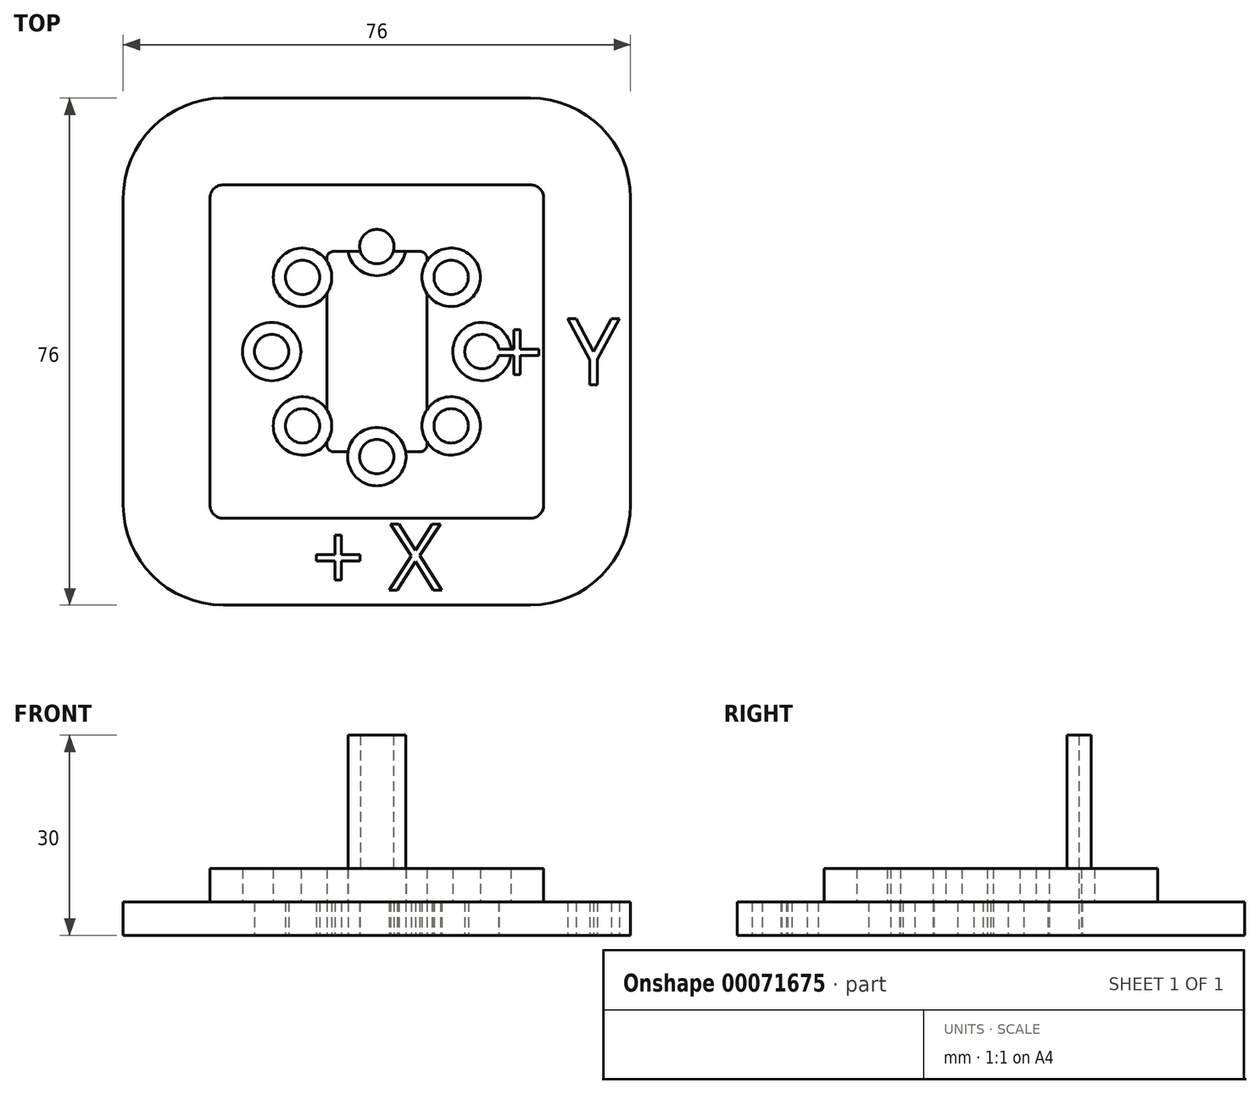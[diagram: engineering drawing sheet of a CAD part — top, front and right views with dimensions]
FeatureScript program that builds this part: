
annotation { "Feature Type Name" : "Feature", "Feature Type Description" : "" }
export const myFeature = defineFeature(function(context is Context, id is Id, definition is map)
    precondition{}
    {
        {
            var Q0;
            Q0=qCreatedBy(makeId("Top.planeOp"),FACE);
            var sketch = newSketch(context, id + "F0", { "sketchPlane" : qUnion([Q0])});
            skLineSegment(sketch, "E0.bottom", {"start": v(-23, 38) * mm, "end": v(23, 38) * mm});
            skLineSegment(sketch, "E0.top", {"start": v(-23, -38) * mm, "end": v(23, -38) * mm});
            skLineSegment(sketch, "E0.left", {"start": v(-38, 23) * mm, "end": v(-38, -23) * mm});
            skLineSegment(sketch, "E0.right", {"start": v(38, 23) * mm, "end": v(38, -23) * mm});
            skLineSegment(sketch, "E1.bottom", {"start": v(-6.5, 15) * mm, "end": v(6.5, 15) * mm});
            skLineSegment(sketch, "E1.top", {"start": v(-6.5, -15) * mm, "end": v(6.5, -15) * mm});
            skLineSegment(sketch, "E1.left", {"start": v(-7.5, 14) * mm, "end": v(-7.5, -14) * mm});
            skLineSegment(sketch, "E1.right", {"start": v(7.5, 14) * mm, "end": v(7.5, -14) * mm});
            skPoint(sketch, "E2.visualSharp", {"position": v(38, 38) * mm});
            skArc(sketch, "E2.filletArc", {"start": v(38, 23) * mm, "mid": v(33.6, 33.6) * mm, "end": v(23, 38) * mm});
            skPoint(sketch, "E3.visualSharp", {"position": v(-38, 38) * mm});
            skArc(sketch, "E3.filletArc", {"start": v(-23, 38) * mm, "mid": v(-33.6, 33.6) * mm, "end": v(-38, 23) * mm});
            skPoint(sketch, "E4.visualSharp", {"position": v(38, -38) * mm});
            skArc(sketch, "E4.filletArc", {"start": v(23, -38) * mm, "mid": v(33.6, -33.6) * mm, "end": v(38, -23) * mm});
            skPoint(sketch, "E5.visualSharp", {"position": v(-38, -38) * mm});
            skArc(sketch, "E5.filletArc", {"start": v(-38, -23) * mm, "mid": v(-33.6, -33.6) * mm, "end": v(-23, -38) * mm});
            skPoint(sketch, "E6.visualSharp", {"position": v(-7.5, 15) * mm});
            skArc(sketch, "E6.filletArc", {"start": v(-6.5, 15) * mm, "mid": v(-7.2, 14.7) * mm, "end": v(-7.5, 14) * mm});
            skPoint(sketch, "E7.visualSharp", {"position": v(7.5, 15) * mm});
            skArc(sketch, "E7.filletArc", {"start": v(7.5, 14) * mm, "mid": v(7.2, 14.7) * mm, "end": v(6.5, 15) * mm});
            skPoint(sketch, "E8.visualSharp", {"position": v(-7.5, -15) * mm});
            skArc(sketch, "E8.filletArc", {"start": v(-7.5, -14) * mm, "mid": v(-7.2, -14.7) * mm, "end": v(-6.5, -15) * mm});
            skPoint(sketch, "E9.visualSharp", {"position": v(7.5, -15) * mm});
            skArc(sketch, "E9.filletArc", {"start": v(6.5, -15) * mm, "mid": v(7.2, -14.7) * mm, "end": v(7.5, -14) * mm});
            skArc(sketch, "E10.0", {"start": v(-6.5, 15.25) * mm, "mid": v(-7.38, 14.88) * mm, "end": v(-7.75, 14) * mm});
            skLineSegment(sketch, "E10.1", {"start": v(-7.75, 14) * mm, "end": v(-7.75, -14) * mm});
            skLineSegment(sketch, "E10.2", {"start": v(-6.5, 15.25) * mm, "end": v(6.5, 15.25) * mm});
            skArc(sketch, "E10.3", {"start": v(-7.75, -14) * mm, "mid": v(-7.38, -14.88) * mm, "end": v(-6.5, -15.25) * mm});
            skArc(sketch, "E10.4", {"start": v(7.75, 14) * mm, "mid": v(7.38, 14.88) * mm, "end": v(6.5, 15.25) * mm});
            skLineSegment(sketch, "E10.5", {"start": v(7.75, 14) * mm, "end": v(7.75, -14) * mm});
            skArc(sketch, "E10.6", {"start": v(6.5, -15.25) * mm, "mid": v(7.38, -14.88) * mm, "end": v(7.75, -14) * mm});
            skLineSegment(sketch, "E10.7", {"start": v(-6.5, -15.25) * mm, "end": v(6.5, -15.25) * mm});
            skArc(sketch, "E11.0", {"start": v(-6.5, 22.75) * mm, "mid": v(-12.69, 20.19) * mm, "end": v(-15.25, 14) * mm});
            skLineSegment(sketch, "E11.1", {"start": v(-15.25, 14) * mm, "end": v(-15.25, -14) * mm});
            skLineSegment(sketch, "E11.2", {"start": v(-6.5, 22.75) * mm, "end": v(6.5, 22.75) * mm});
            skArc(sketch, "E11.3", {"start": v(-15.25, -14) * mm, "mid": v(-12.69, -20.19) * mm, "end": v(-6.5, -22.75) * mm});
            skArc(sketch, "E11.4", {"start": v(15.25, 14) * mm, "mid": v(12.69, 20.19) * mm, "end": v(6.5, 22.75) * mm});
            skLineSegment(sketch, "E11.5", {"start": v(15.25, 14) * mm, "end": v(15.25, -14) * mm});
            skArc(sketch, "E11.6", {"start": v(6.5, -22.75) * mm, "mid": v(12.69, -20.19) * mm, "end": v(15.25, -14) * mm});
            skLineSegment(sketch, "E11.7", {"start": v(-6.5, -22.75) * mm, "end": v(6.5, -22.75) * mm});
            skText(sketch, "E12", { "text": "+ X", "fontName": "OpenSans-Regular.ttf"});
            skText(sketch, "E13", { "text": "+ Y", "fontName": "OpenSans-Regular.ttf"});
            skCircle(sketch, "E14", {"center": v(0, 0) * mm, "radius": 15.75 * mm, "construction": true});
            skCircle(sketch, "E15", {"center": v(0, 15.75) * mm, "radius": 2.58 * mm});
            skCircle(sketch, "E16.1.0", {"center": v(-11.14, 11.14) * mm, "radius": 2.58 * mm});
            skCircle(sketch, "E16.2.0", {"center": v(-15.75, 0) * mm, "radius": 2.58 * mm});
            skCircle(sketch, "E16.3.0", {"center": v(-11.14, -11.14) * mm, "radius": 2.58 * mm});
            skCircle(sketch, "E16.4.0", {"center": v(0, -15.75) * mm, "radius": 2.58 * mm});
            skCircle(sketch, "E16.5.0", {"center": v(11.14, -11.14) * mm, "radius": 2.58 * mm});
            skCircle(sketch, "E16.6.0", {"center": v(15.75, 0) * mm, "radius": 2.58 * mm});
            skCircle(sketch, "E16.7.0", {"center": v(11.14, 11.14) * mm, "radius": 2.58 * mm});
            skCircle(sketch, "E17", {"center": v(0, 15.75) * mm, "radius": 4.38 * mm});
            skCircle(sketch, "E18.1.0", {"center": v(-11.14, 11.14) * mm, "radius": 4.38 * mm});
            skCircle(sketch, "E18.2.0", {"center": v(-15.75, 0) * mm, "radius": 4.38 * mm});
            skCircle(sketch, "E18.3.0", {"center": v(-11.14, -11.14) * mm, "radius": 4.38 * mm});
            skCircle(sketch, "E18.4.0", {"center": v(0, -15.75) * mm, "radius": 4.38 * mm});
            skCircle(sketch, "E18.5.0", {"center": v(11.14, -11.14) * mm, "radius": 4.38 * mm});
            skCircle(sketch, "E18.6.0", {"center": v(15.75, 0) * mm, "radius": 4.38 * mm});
            skCircle(sketch, "E18.7.0", {"center": v(11.14, 11.14) * mm, "radius": 4.38 * mm});
            skLineSegment(sketch, "E19.0", {"start": v(-23, 25) * mm, "end": v(23, 25) * mm});
            skArc(sketch, "E19.1", {"start": v(25, 23) * mm, "mid": v(24.41, 24.41) * mm, "end": v(23, 25) * mm});
            skArc(sketch, "E19.2", {"start": v(-23, 25) * mm, "mid": v(-24.41, 24.41) * mm, "end": v(-25, 23) * mm});
            skLineSegment(sketch, "E19.3", {"start": v(25, 23) * mm, "end": v(25, -23) * mm});
            skLineSegment(sketch, "E19.4", {"start": v(-25, 23) * mm, "end": v(-25, -23) * mm});
            skArc(sketch, "E19.5", {"start": v(-25, -23) * mm, "mid": v(-24.41, -24.41) * mm, "end": v(-23, -25) * mm});
            skLineSegment(sketch, "E19.6", {"start": v(-23, -25) * mm, "end": v(23, -25) * mm});
            skArc(sketch, "E19.7", {"start": v(23, -25) * mm, "mid": v(24.41, -24.41) * mm, "end": v(25, -23) * mm});
            const initialGuessF0  = {"E12": [-0.00976, -0.0358, 1, 0, 0.01], "E13": [0.01704, -0.005, 1, 0, 0.01]};
            skSetInitialGuess(sketch, initialGuessF0);
            skSolve(sketch);
        }
        {
            var Q0;
            Q0=makeQuery(id+"F0.imprint","IMPRINT",FACE,{"disambiguationData":[TD([[makeQuery(id+"F0.imprint","IMPRINT",EDGE,{"derivedFrom":sQuery(id+"F0.wireOp",EDGE,"E0.bottom")}),-1.0]])]});
            var Q1;
            {var subQ9=sQuery(id+"F0.wireOp",EDGE,"E10.0");Q1=makeQuery(id+"F0.imprint","IMPRINT",FACE,{"disambiguationData":[TD([[makeQuery(id+"F0.imprint","IMPRINT",EDGE,{"derivedFrom":subQ9}),-1.0]])]});}
            var Q2;
            Q2=makeQuery(id+"F0.imprint","IMPRINT",FACE,{"disambiguationData":[TD([[makeQuery(id+"F0.imprint","IMPRINT",EDGE,{"derivedFrom":sQuery(id+"F0.wireOp",EDGE,"E1.right")}),1.0]])]});
            var Q3;
            Q3=makeQuery(id+"F0.imprint","IMPRINT",FACE,{"disambiguationData":[TD([[makeQuery(id+"F0.imprint","IMPRINT",EDGE,{"derivedFrom":sQuery(id+"F0.wireOp",EDGE,"E1.left")}),-1.0]])]});
            var Q4;
            Q4=makeQuery(id+"F0.imprint","IMPRINT",FACE,{"disambiguationData":[TD([[makeQuery(id+"F0.imprint","IMPRINT",EDGE,{"derivedFrom":sQuery(id+"F0.wireOp",EDGE,"E1.left")}),1.0]])]});
            var Q5;
            {var subQ0=sQuery(id+"F0.wireOp",EDGE,"E17");var subQ1=sQuery(id+"F0.wireOp",EDGE,"E10.2");var subQ2=makeQuery(id+"F0.imprint","INTERSECT",VERTEX,{"disambiguationData":[OD(0.0)],"derivedFrom":[subQ1,subQ0]});Q5=makeQuery(id+"F0.imprint","IMPRINT",FACE,{"disambiguationData":[TD([[makeQuery(id+"F0.imprint","IMPRINT",EDGE,{"disambiguationData":[TD([[subQ2,-1.0]])],"derivedFrom":subQ1}),1.0]])]});}
            var Q6;
            {var subQ0=sQuery(id+"F0.wireOp",EDGE,"E15");var subQ1=sQuery(id+"F0.wireOp",EDGE,"E10.2");var subQ2=makeQuery(id+"F0.imprint","INTERSECT",VERTEX,{"disambiguationData":[OD(0.0)],"derivedFrom":[subQ1,subQ0]});Q6=makeQuery(id+"F0.imprint","IMPRINT",FACE,{"disambiguationData":[TD([[makeQuery(id+"F0.imprint","IMPRINT",EDGE,{"disambiguationData":[TD([[subQ2,-1.0]])],"derivedFrom":subQ1}),1.0]])]});}
            var Q7;
            {var subQ0=sQuery(id+"F0.wireOp",EDGE,"E17");var subQ1=sQuery(id+"F0.wireOp",EDGE,"E1.bottom");var subQ2=makeQuery(id+"F0.imprint","INTERSECT",VERTEX,{"disambiguationData":[OD(0.0)],"derivedFrom":[subQ1,subQ0]});Q7=makeQuery(id+"F0.imprint","IMPRINT",FACE,{"disambiguationData":[TD([[makeQuery(id+"F0.imprint","IMPRINT",EDGE,{"disambiguationData":[TD([[subQ2,-1.0]])],"derivedFrom":subQ1}),-1.0]])]});}
            var Q8;
            Q8=makeQuery(id+"F0.imprint","IMPRINT",FACE,{"disambiguationData":[TD([[makeQuery(id+"F0.imprint","IMPRINT",EDGE,{"derivedFrom":sQuery(id+"F0.wireOp",EDGE,"E16.7.0")}),1.0]])]});
            var Q9;
            Q9=makeQuery(id+"F0.imprint","IMPRINT",FACE,{"disambiguationData":[TD([[makeQuery(id+"F0.imprint","IMPRINT",EDGE,{"derivedFrom":sQuery(id+"F0.wireOp",EDGE,"E16.7.0")}),-1.0]])]});
            var Q10;
            {var subQ1=sQuery(id+"F0.wireOp",EDGE,"E10.5");var subQ5=sQuery(id+"F0.wireOp",EDGE,"E18.7.0");var subQ6=makeQuery(id+"F0.imprint","INTERSECT",VERTEX,{"disambiguationData":[OD(1.0)],"derivedFrom":[subQ1,subQ5]});Q10=makeQuery(id+"F0.imprint","IMPRINT",FACE,{"disambiguationData":[TD([[makeQuery(id+"F0.imprint","IMPRINT",EDGE,{"disambiguationData":[TD([[subQ6,-1.0]])],"derivedFrom":subQ1}),1.0]])]});}
            var Q11;
            Q11=makeQuery(id+"F0.imprint","IMPRINT",FACE,{"disambiguationData":[TD([[makeQuery(id+"F0.imprint","IMPRINT",EDGE,{"derivedFrom":sQuery(id+"F0.wireOp",EDGE,"E16.1.0")}),-1.0]])]});
            var Q12;
            Q12=makeQuery(id+"F0.imprint","IMPRINT",FACE,{"disambiguationData":[TD([[makeQuery(id+"F0.imprint","IMPRINT",EDGE,{"derivedFrom":sQuery(id+"F0.wireOp",EDGE,"E16.1.0")}),1.0]])]});
            var Q13;
            {var subQ0=sQuery(id+"F0.wireOp",EDGE,"E18.1.0");var subQ1=sQuery(id+"F0.wireOp",EDGE,"E10.1");var subQ2=makeQuery(id+"F0.imprint","INTERSECT",VERTEX,{"disambiguationData":[OD(1.0)],"derivedFrom":[subQ1,subQ0]});Q13=makeQuery(id+"F0.imprint","IMPRINT",FACE,{"disambiguationData":[TD([[makeQuery(id+"F0.imprint","IMPRINT",EDGE,{"disambiguationData":[TD([[subQ2,-1.0]])],"derivedFrom":subQ1}),-1.0]])]});}
            var Q14;
            {var subQ0=sQuery(id+"F0.wireOp",EDGE,"E18.2.0");var subQ1=sQuery(id+"F0.wireOp",EDGE,"E11.1");var subQ2=makeQuery(id+"F0.imprint","INTERSECT",VERTEX,{"disambiguationData":[OD(0.0)],"derivedFrom":[subQ1,subQ0]});Q14=makeQuery(id+"F0.imprint","IMPRINT",FACE,{"disambiguationData":[TD([[makeQuery(id+"F0.imprint","IMPRINT",EDGE,{"disambiguationData":[TD([[subQ2,-1.0]])],"derivedFrom":subQ1}),1.0]])]});}
            var Q15;
            {var subQ0=sQuery(id+"F0.wireOp",EDGE,"E16.2.0");var subQ1=sQuery(id+"F0.wireOp",EDGE,"E11.1");var subQ2=makeQuery(id+"F0.imprint","INTERSECT",VERTEX,{"disambiguationData":[OD(0.0)],"derivedFrom":[subQ1,subQ0]});Q15=makeQuery(id+"F0.imprint","IMPRINT",FACE,{"disambiguationData":[TD([[makeQuery(id+"F0.imprint","IMPRINT",EDGE,{"disambiguationData":[TD([[subQ2,-1.0]])],"derivedFrom":subQ1}),1.0]])]});}
            var Q16;
            {var subQ0=sQuery(id+"F0.wireOp",EDGE,"E16.2.0");var subQ1=sQuery(id+"F0.wireOp",EDGE,"E11.1");var subQ2=makeQuery(id+"F0.imprint","INTERSECT",VERTEX,{"disambiguationData":[OD(0.0)],"derivedFrom":[subQ1,subQ0]});Q16=makeQuery(id+"F0.imprint","IMPRINT",FACE,{"disambiguationData":[TD([[makeQuery(id+"F0.imprint","IMPRINT",EDGE,{"disambiguationData":[TD([[subQ2,-1.0]])],"derivedFrom":subQ1}),-1.0]])]});}
            var Q17;
            {var subQ0=sQuery(id+"F0.wireOp",EDGE,"E18.2.0");var subQ1=sQuery(id+"F0.wireOp",EDGE,"E11.1");var subQ2=makeQuery(id+"F0.imprint","INTERSECT",VERTEX,{"disambiguationData":[OD(0.0)],"derivedFrom":[subQ1,subQ0]});Q17=makeQuery(id+"F0.imprint","IMPRINT",FACE,{"disambiguationData":[TD([[makeQuery(id+"F0.imprint","IMPRINT",EDGE,{"disambiguationData":[TD([[subQ2,-1.0]])],"derivedFrom":subQ1}),-1.0]])]});}
            var Q18;
            Q18=makeQuery(id+"F0.imprint","IMPRINT",FACE,{"disambiguationData":[TD([[makeQuery(id+"F0.imprint","IMPRINT",EDGE,{"derivedFrom":sQuery(id+"F0.wireOp",EDGE,"E16.3.0")}),-1.0]])]});
            var Q19;
            Q19=makeQuery(id+"F0.imprint","IMPRINT",FACE,{"disambiguationData":[TD([[makeQuery(id+"F0.imprint","IMPRINT",EDGE,{"derivedFrom":sQuery(id+"F0.wireOp",EDGE,"E16.3.0")}),1.0]])]});
            var Q20;
            {var subQ1=sQuery(id+"F0.wireOp",EDGE,"E10.3");Q20=makeQuery(id+"F0.imprint","IMPRINT",FACE,{"disambiguationData":[TD([[makeQuery(id+"F0.imprint","IMPRINT",EDGE,{"derivedFrom":subQ1}),-1.0]])]});}
            var Q21;
            {var subQ0=sQuery(id+"F0.wireOp",EDGE,"E18.4.0");var subQ1=sQuery(id+"F0.wireOp",EDGE,"E10.7");var subQ2=makeQuery(id+"F0.imprint","INTERSECT",VERTEX,{"disambiguationData":[OD(0.0)],"derivedFrom":[subQ1,subQ0]});Q21=makeQuery(id+"F0.imprint","IMPRINT",FACE,{"disambiguationData":[TD([[makeQuery(id+"F0.imprint","IMPRINT",EDGE,{"disambiguationData":[TD([[subQ2,-1.0]])],"derivedFrom":subQ1}),-1.0]])]});}
            var Q22;
            {var subQ0=sQuery(id+"F0.wireOp",EDGE,"E18.4.0");var subQ1=sQuery(id+"F0.wireOp",EDGE,"E1.top");var subQ2=makeQuery(id+"F0.imprint","INTERSECT",VERTEX,{"disambiguationData":[OD(0.0)],"derivedFrom":[subQ1,subQ0]});Q22=makeQuery(id+"F0.imprint","IMPRINT",FACE,{"disambiguationData":[TD([[makeQuery(id+"F0.imprint","IMPRINT",EDGE,{"disambiguationData":[TD([[subQ2,-1.0]])],"derivedFrom":subQ1}),1.0]])]});}
            var Q23;
            {var subQ0=sQuery(id+"F0.wireOp",EDGE,"E16.4.0");var subQ1=sQuery(id+"F0.wireOp",EDGE,"E1.top");var subQ2=makeQuery(id+"F0.imprint","INTERSECT",VERTEX,{"disambiguationData":[OD(0.0)],"derivedFrom":[subQ1,subQ0]});Q23=makeQuery(id+"F0.imprint","IMPRINT",FACE,{"disambiguationData":[TD([[makeQuery(id+"F0.imprint","IMPRINT",EDGE,{"disambiguationData":[TD([[subQ2,-1.0]])],"derivedFrom":subQ1}),1.0]])]});}
            var Q24;
            {var subQ0=sQuery(id+"F0.wireOp",EDGE,"E16.4.0");var subQ1=sQuery(id+"F0.wireOp",EDGE,"E10.7");var subQ2=makeQuery(id+"F0.imprint","INTERSECT",VERTEX,{"disambiguationData":[OD(0.0)],"derivedFrom":[subQ1,subQ0]});Q24=makeQuery(id+"F0.imprint","IMPRINT",FACE,{"disambiguationData":[TD([[makeQuery(id+"F0.imprint","IMPRINT",EDGE,{"disambiguationData":[TD([[subQ2,-1.0]])],"derivedFrom":subQ1}),-1.0]])]});}
            var Q25;
            Q25=makeQuery(id+"F0.imprint","IMPRINT",FACE,{"disambiguationData":[TD([[makeQuery(id+"F0.imprint","IMPRINT",EDGE,{"derivedFrom":sQuery(id+"F0.wireOp",EDGE,"E16.5.0")}),-1.0]])]});
            var Q26;
            Q26=makeQuery(id+"F0.imprint","IMPRINT",FACE,{"disambiguationData":[TD([[makeQuery(id+"F0.imprint","IMPRINT",EDGE,{"derivedFrom":sQuery(id+"F0.wireOp",EDGE,"E16.5.0")}),1.0]])]});
            var Q27;
            {var subQ0=sQuery(id+"F0.wireOp",EDGE,"E16.6.0");var subQ1=sQuery(id+"F0.wireOp",EDGE,"E11.5");var subQ2=makeQuery(id+"F0.imprint","INTERSECT",VERTEX,{"disambiguationData":[OD(1.0)],"derivedFrom":[subQ1,subQ0]});Q27=makeQuery(id+"F0.imprint","IMPRINT",FACE,{"disambiguationData":[TD([[makeQuery(id+"F0.imprint","IMPRINT",EDGE,{"disambiguationData":[TD([[subQ2,-1.0]])],"derivedFrom":subQ1}),1.0]])]});}
            var Q28;
            {var subQ1=sQuery(id+"F0.wireOp",EDGE,"E13.sketch_text.stroke-7");Q28=makeQuery(id+"F0.imprint","IMPRINT",FACE,{"disambiguationData":[TD([[makeQuery(id+"F0.imprint","IMPRINT",EDGE,{"derivedFrom":subQ1}),1.0]])]});}
            var Q29;
            {var subQ0=sQuery(id+"F0.wireOp",EDGE,"E18.6.0");var subQ1=sQuery(id+"F0.wireOp",EDGE,"E11.5");var subQ2=makeQuery(id+"F0.imprint","INTERSECT",VERTEX,{"disambiguationData":[OD(0.0)],"derivedFrom":[subQ1,subQ0]});Q29=makeQuery(id+"F0.imprint","IMPRINT",FACE,{"disambiguationData":[TD([[makeQuery(id+"F0.imprint","IMPRINT",EDGE,{"disambiguationData":[TD([[subQ2,-1.0]])],"derivedFrom":subQ1}),1.0]])]});}
            var Q30;
            {var subQ0=sQuery(id+"F0.wireOp",EDGE,"E18.6.0");var subQ1=sQuery(id+"F0.wireOp",EDGE,"E11.5");var subQ2=makeQuery(id+"F0.imprint","INTERSECT",VERTEX,{"disambiguationData":[OD(0.0)],"derivedFrom":[subQ1,subQ0]});Q30=makeQuery(id+"F0.imprint","IMPRINT",FACE,{"disambiguationData":[TD([[makeQuery(id+"F0.imprint","IMPRINT",EDGE,{"disambiguationData":[TD([[subQ2,-1.0]])],"derivedFrom":subQ1}),-1.0]])]});}
            var Q31;
            {var subQ0=sQuery(id+"F0.wireOp",EDGE,"E16.6.0");var subQ1=sQuery(id+"F0.wireOp",EDGE,"E11.5");var subQ2=makeQuery(id+"F0.imprint","INTERSECT",VERTEX,{"disambiguationData":[OD(0.0)],"derivedFrom":[subQ1,subQ0]});Q31=makeQuery(id+"F0.imprint","IMPRINT",FACE,{"disambiguationData":[TD([[makeQuery(id+"F0.imprint","IMPRINT",EDGE,{"disambiguationData":[TD([[subQ2,-1.0]])],"derivedFrom":subQ1}),-1.0]])]});}
            var Q32;
            {var subQ0=sQuery(id+"F0.wireOp",EDGE,"E18.3.0");var subQ1=sQuery(id+"F0.wireOp",EDGE,"E1.left");var subQ2=makeQuery(id+"F0.imprint","INTERSECT",VERTEX,{"disambiguationData":[OD(0.0)],"derivedFrom":[subQ1,subQ0]});Q32=makeQuery(id+"F0.imprint","IMPRINT",FACE,{"disambiguationData":[TD([[makeQuery(id+"F0.imprint","IMPRINT",EDGE,{"disambiguationData":[TD([[subQ2,-1.0]])],"derivedFrom":subQ1}),1.0]])]});}
            var Q33;
            {var subQ0=sQuery(id+"F0.wireOp",EDGE,"E18.5.0");var subQ1=sQuery(id+"F0.wireOp",EDGE,"E1.right");var subQ2=makeQuery(id+"F0.imprint","INTERSECT",VERTEX,{"disambiguationData":[OD(0.0)],"derivedFrom":[subQ1,subQ0]});Q33=makeQuery(id+"F0.imprint","IMPRINT",FACE,{"disambiguationData":[TD([[makeQuery(id+"F0.imprint","IMPRINT",EDGE,{"disambiguationData":[TD([[subQ2,-1.0]])],"derivedFrom":subQ1}),-1.0]])]});}
            var Q34;
            {var subQ0=sQuery(id+"F0.wireOp",EDGE,"E18.7.0");var subQ1=sQuery(id+"F0.wireOp",EDGE,"E1.right");var subQ2=makeQuery(id+"F0.imprint","INTERSECT",VERTEX,{"disambiguationData":[OD(0.0)],"derivedFrom":[subQ1,subQ0]});Q34=makeQuery(id+"F0.imprint","IMPRINT",FACE,{"disambiguationData":[TD([[makeQuery(id+"F0.imprint","IMPRINT",EDGE,{"disambiguationData":[TD([[subQ2,-1.0]])],"derivedFrom":subQ1}),-1.0]])]});}
            var Q35;
            {var subQ0=sQuery(id+"F0.wireOp",EDGE,"E18.1.0");var subQ1=sQuery(id+"F0.wireOp",EDGE,"E1.left");var subQ2=makeQuery(id+"F0.imprint","INTERSECT",VERTEX,{"disambiguationData":[OD(0.0)],"derivedFrom":[subQ1,subQ0]});Q35=makeQuery(id+"F0.imprint","IMPRINT",FACE,{"disambiguationData":[TD([[makeQuery(id+"F0.imprint","IMPRINT",EDGE,{"disambiguationData":[TD([[subQ2,-1.0]])],"derivedFrom":subQ1}),1.0]])]});}
            var Q36;
            {var subQ1=sQuery(id+"F0.wireOp",EDGE,"E6.filletArc");Q36=makeQuery(id+"F0.imprint","IMPRINT",FACE,{"disambiguationData":[TD([[makeQuery(id+"F0.imprint","IMPRINT",EDGE,{"derivedFrom":subQ1}),-1.0]])]});}
            var Q37;
            {var subQ0=sQuery(id+"F0.wireOp",EDGE,"E17");var subQ1=sQuery(id+"F0.wireOp",EDGE,"E1.bottom");var subQ2=makeQuery(id+"F0.imprint","INTERSECT",VERTEX,{"disambiguationData":[OD(0.0)],"derivedFrom":[subQ1,subQ0]});Q37=makeQuery(id+"F0.imprint","IMPRINT",FACE,{"disambiguationData":[TD([[makeQuery(id+"F0.imprint","IMPRINT",EDGE,{"disambiguationData":[TD([[subQ2,-1.0]])],"derivedFrom":subQ1}),1.0]])]});}
            var Q38;
            {var subQ0=sQuery(id+"F0.wireOp",EDGE,"E15");var subQ1=sQuery(id+"F0.wireOp",EDGE,"E1.bottom");var subQ2=makeQuery(id+"F0.imprint","INTERSECT",VERTEX,{"disambiguationData":[OD(0.0)],"derivedFrom":[subQ1,subQ0]});Q38=makeQuery(id+"F0.imprint","IMPRINT",FACE,{"disambiguationData":[TD([[makeQuery(id+"F0.imprint","IMPRINT",EDGE,{"disambiguationData":[TD([[subQ2,-1.0]])],"derivedFrom":subQ1}),1.0]])]});}
            var Q39;
            {var subQ0=sQuery(id+"F0.wireOp",EDGE,"E15");var subQ1=sQuery(id+"F0.wireOp",EDGE,"E1.bottom");var subQ2=makeQuery(id+"F0.imprint","INTERSECT",VERTEX,{"disambiguationData":[OD(0.0)],"derivedFrom":[subQ1,subQ0]});Q39=makeQuery(id+"F0.imprint","IMPRINT",FACE,{"disambiguationData":[TD([[makeQuery(id+"F0.imprint","IMPRINT",EDGE,{"disambiguationData":[TD([[subQ2,-1.0]])],"derivedFrom":subQ1}),-1.0]])]});}
            var Q40;
            {var subQ0=sQuery(id+"F0.wireOp",EDGE,"E15");var subQ1=sQuery(id+"F0.wireOp",EDGE,"E1.bottom");var subQ2=makeQuery(id+"F0.imprint","INTERSECT",VERTEX,{"disambiguationData":[OD(1.0)],"derivedFrom":[subQ1,subQ0]});Q40=makeQuery(id+"F0.imprint","IMPRINT",FACE,{"disambiguationData":[TD([[makeQuery(id+"F0.imprint","IMPRINT",EDGE,{"disambiguationData":[TD([[subQ2,-1.0]])],"derivedFrom":subQ1}),1.0]])]});}
            var Q41;
            {var subQ6=sQuery(id+"F0.wireOp",EDGE,"E7.filletArc");Q41=makeQuery(id+"F0.imprint","IMPRINT",FACE,{"disambiguationData":[TD([[makeQuery(id+"F0.imprint","IMPRINT",EDGE,{"derivedFrom":subQ6}),-1.0]])]});}
            var Q42;
            {var subQ0=sQuery(id+"F0.wireOp",EDGE,"E18.1.0");var subQ1=sQuery(id+"F0.wireOp",EDGE,"E11.1");var subQ2=makeQuery(id+"F0.imprint","INTERSECT",VERTEX,{"disambiguationData":[OD(0.0)],"derivedFrom":[subQ1,subQ0]});Q42=makeQuery(id+"F0.imprint","IMPRINT",FACE,{"disambiguationData":[TD([[makeQuery(id+"F0.imprint","IMPRINT",EDGE,{"disambiguationData":[TD([[subQ2,-1.0]])],"derivedFrom":subQ1}),-1.0]])]});}
            var Q43;
            {var subQ0=sQuery(id+"F0.wireOp",EDGE,"E18.7.0");var subQ1=sQuery(id+"F0.wireOp",EDGE,"E11.5");var subQ2=makeQuery(id+"F0.imprint","INTERSECT",VERTEX,{"disambiguationData":[OD(0.0)],"derivedFrom":[subQ1,subQ0]});Q43=makeQuery(id+"F0.imprint","IMPRINT",FACE,{"disambiguationData":[TD([[makeQuery(id+"F0.imprint","IMPRINT",EDGE,{"disambiguationData":[TD([[subQ2,-1.0]])],"derivedFrom":subQ1}),1.0]])]});}
            var Q44;
            {var subQ0=sQuery(id+"F0.wireOp",EDGE,"E18.3.0");var subQ1=sQuery(id+"F0.wireOp",EDGE,"E11.1");var subQ2=makeQuery(id+"F0.imprint","INTERSECT",VERTEX,{"disambiguationData":[OD(0.0)],"derivedFrom":[subQ1,subQ0]});Q44=makeQuery(id+"F0.imprint","IMPRINT",FACE,{"disambiguationData":[TD([[makeQuery(id+"F0.imprint","IMPRINT",EDGE,{"disambiguationData":[TD([[subQ2,-1.0]])],"derivedFrom":subQ1}),-1.0]])]});}
            var Q45;
            {var subQ4=sQuery(id+"F0.wireOp",EDGE,"E8.filletArc");Q45=makeQuery(id+"F0.imprint","IMPRINT",FACE,{"disambiguationData":[TD([[makeQuery(id+"F0.imprint","IMPRINT",EDGE,{"derivedFrom":subQ4}),-1.0]])]});}
            var Q46;
            {var subQ0=sQuery(id+"F0.wireOp",EDGE,"E18.4.0");var subQ1=sQuery(id+"F0.wireOp",EDGE,"E1.top");var subQ2=makeQuery(id+"F0.imprint","INTERSECT",VERTEX,{"disambiguationData":[OD(0.0)],"derivedFrom":[subQ1,subQ0]});Q46=makeQuery(id+"F0.imprint","IMPRINT",FACE,{"disambiguationData":[TD([[makeQuery(id+"F0.imprint","IMPRINT",EDGE,{"disambiguationData":[TD([[subQ2,-1.0]])],"derivedFrom":subQ1}),-1.0]])]});}
            var Q47;
            {var subQ0=sQuery(id+"F0.wireOp",EDGE,"E16.4.0");var subQ1=sQuery(id+"F0.wireOp",EDGE,"E1.top");var subQ2=makeQuery(id+"F0.imprint","INTERSECT",VERTEX,{"disambiguationData":[OD(0.0)],"derivedFrom":[subQ1,subQ0]});Q47=makeQuery(id+"F0.imprint","IMPRINT",FACE,{"disambiguationData":[TD([[makeQuery(id+"F0.imprint","IMPRINT",EDGE,{"disambiguationData":[TD([[subQ2,-1.0]])],"derivedFrom":subQ1}),-1.0]])]});}
            var Q48;
            {var subQ0=sQuery(id+"F0.wireOp",EDGE,"E16.4.0");var subQ1=sQuery(id+"F0.wireOp",EDGE,"E1.top");var subQ2=makeQuery(id+"F0.imprint","INTERSECT",VERTEX,{"disambiguationData":[OD(1.0)],"derivedFrom":[subQ1,subQ0]});Q48=makeQuery(id+"F0.imprint","IMPRINT",FACE,{"disambiguationData":[TD([[makeQuery(id+"F0.imprint","IMPRINT",EDGE,{"disambiguationData":[TD([[subQ2,-1.0]])],"derivedFrom":subQ1}),-1.0]])]});}
            var Q49;
            {var subQ0=sQuery(id+"F0.wireOp",EDGE,"E18.5.0");var subQ1=sQuery(id+"F0.wireOp",EDGE,"E11.5");var subQ2=makeQuery(id+"F0.imprint","INTERSECT",VERTEX,{"disambiguationData":[OD(0.0)],"derivedFrom":[subQ1,subQ0]});Q49=makeQuery(id+"F0.imprint","IMPRINT",FACE,{"disambiguationData":[TD([[makeQuery(id+"F0.imprint","IMPRINT",EDGE,{"disambiguationData":[TD([[subQ2,-1.0]])],"derivedFrom":subQ1}),1.0]])]});}
            var Q50;
            {var subQ4=sQuery(id+"F0.wireOp",EDGE,"E9.filletArc");Q50=makeQuery(id+"F0.imprint","IMPRINT",FACE,{"disambiguationData":[TD([[makeQuery(id+"F0.imprint","IMPRINT",EDGE,{"derivedFrom":subQ4}),-1.0]])]});}
            var Q51;
            {var subQ21=sQuery(id+"F0.wireOp",EDGE,"E11.0");Q51=makeQuery(id+"F0.imprint","IMPRINT",FACE,{"disambiguationData":[TD([[makeQuery(id+"F0.imprint","IMPRINT",EDGE,{"derivedFrom":subQ21}),-1.0]])]});}
            extrude(context, id + "F1", {"entities" : qUnion([Q0, Q1, Q2, Q3, Q4, Q5, Q6, Q7, Q8, Q9, Q10, Q11, Q12, Q13, Q14, Q15, Q16, Q17, Q18, Q19, Q20, Q21, Q22, Q23, Q24, Q25, Q26, Q27, Q28, Q29, Q30, Q31, Q32, Q33, Q34, Q35, Q36, Q37, Q38, Q39, Q40, Q41, Q42, Q43, Q44, Q45, Q46, Q47, Q48, Q49, Q50, Q51]), "depth" : 10 * mm});
        }
        {
            var Q0;
            {var subQ0=sQuery(id+"F0.wireOp",EDGE,"E15");var subQ1=sQuery(id+"F0.wireOp",EDGE,"E1.bottom");var subQ2=makeQuery(id+"F0.imprint","INTERSECT",VERTEX,{"disambiguationData":[OD(0.0)],"derivedFrom":[subQ1,subQ0]});Q0=makeQuery(id+"F0.imprint","IMPRINT",FACE,{"disambiguationData":[TD([[makeQuery(id+"F0.imprint","IMPRINT",EDGE,{"disambiguationData":[TD([[subQ2,-1.0]])],"derivedFrom":subQ1}),-1.0]])]});}
            var Q1;
            {var subQ0=sQuery(id+"F0.wireOp",EDGE,"E15");var subQ1=sQuery(id+"F0.wireOp",EDGE,"E10.2");var subQ2=makeQuery(id+"F0.imprint","INTERSECT",VERTEX,{"disambiguationData":[OD(0.0)],"derivedFrom":[subQ1,subQ0]});Q1=makeQuery(id+"F0.imprint","IMPRINT",FACE,{"disambiguationData":[TD([[makeQuery(id+"F0.imprint","IMPRINT",EDGE,{"disambiguationData":[TD([[subQ2,-1.0]])],"derivedFrom":subQ1}),1.0]])]});}
            var Q2;
            {var subQ0=sQuery(id+"F0.wireOp",EDGE,"E15");var subQ1=sQuery(id+"F0.wireOp",EDGE,"E1.bottom");var subQ2=makeQuery(id+"F0.imprint","INTERSECT",VERTEX,{"disambiguationData":[OD(0.0)],"derivedFrom":[subQ1,subQ0]});Q2=makeQuery(id+"F0.imprint","IMPRINT",FACE,{"disambiguationData":[TD([[makeQuery(id+"F0.imprint","IMPRINT",EDGE,{"disambiguationData":[TD([[subQ2,-1.0]])],"derivedFrom":subQ1}),1.0]])]});}
            var Q3;
            Q3=makeQuery(id+"F0.imprint","IMPRINT",FACE,{"disambiguationData":[TD([[makeQuery(id+"F0.imprint","IMPRINT",EDGE,{"derivedFrom":sQuery(id+"F0.wireOp",EDGE,"E16.1.0")}),1.0]])]});
            var Q4;
            {var subQ0=sQuery(id+"F0.wireOp",EDGE,"E16.2.0");var subQ1=sQuery(id+"F0.wireOp",EDGE,"E11.1");var subQ2=makeQuery(id+"F0.imprint","INTERSECT",VERTEX,{"disambiguationData":[OD(0.0)],"derivedFrom":[subQ1,subQ0]});Q4=makeQuery(id+"F0.imprint","IMPRINT",FACE,{"disambiguationData":[TD([[makeQuery(id+"F0.imprint","IMPRINT",EDGE,{"disambiguationData":[TD([[subQ2,-1.0]])],"derivedFrom":subQ1}),-1.0]])]});}
            var Q5;
            {var subQ0=sQuery(id+"F0.wireOp",EDGE,"E16.2.0");var subQ1=sQuery(id+"F0.wireOp",EDGE,"E11.1");var subQ2=makeQuery(id+"F0.imprint","INTERSECT",VERTEX,{"disambiguationData":[OD(0.0)],"derivedFrom":[subQ1,subQ0]});Q5=makeQuery(id+"F0.imprint","IMPRINT",FACE,{"disambiguationData":[TD([[makeQuery(id+"F0.imprint","IMPRINT",EDGE,{"disambiguationData":[TD([[subQ2,-1.0]])],"derivedFrom":subQ1}),1.0]])]});}
            var Q6;
            Q6=makeQuery(id+"F0.imprint","IMPRINT",FACE,{"disambiguationData":[TD([[makeQuery(id+"F0.imprint","IMPRINT",EDGE,{"derivedFrom":sQuery(id+"F0.wireOp",EDGE,"E16.7.0")}),1.0]])]});
            var Q7;
            {var subQ1=sQuery(id+"F0.wireOp",EDGE,"E13.sketch_text.stroke-7");Q7=makeQuery(id+"F0.imprint","IMPRINT",FACE,{"disambiguationData":[TD([[makeQuery(id+"F0.imprint","IMPRINT",EDGE,{"derivedFrom":subQ1}),1.0]])]});}
            var Q8;
            {var subQ0=sQuery(id+"F0.wireOp",EDGE,"E16.6.0");var subQ1=sQuery(id+"F0.wireOp",EDGE,"E11.5");var subQ2=makeQuery(id+"F0.imprint","INTERSECT",VERTEX,{"disambiguationData":[OD(0.0)],"derivedFrom":[subQ1,subQ0]});Q8=makeQuery(id+"F0.imprint","IMPRINT",FACE,{"disambiguationData":[TD([[makeQuery(id+"F0.imprint","IMPRINT",EDGE,{"disambiguationData":[TD([[subQ2,-1.0]])],"derivedFrom":subQ1}),-1.0]])]});}
            var Q9;
            {var subQ0=sQuery(id+"F0.wireOp",EDGE,"E13.sketch_text.stroke-7");Q9=makeQuery(id+"F0.imprint","IMPRINT",FACE,{"disambiguationData":[TD([[makeQuery(id+"F0.imprint","IMPRINT",EDGE,{"derivedFrom":subQ0}),-1.0]])]});}
            var Q10;
            Q10=makeQuery(id+"F0.imprint","IMPRINT",FACE,{"disambiguationData":[TD([[makeQuery(id+"F0.imprint","IMPRINT",EDGE,{"derivedFrom":sQuery(id+"F0.wireOp",EDGE,"E16.5.0")}),1.0]])]});
            var Q11;
            Q11=makeQuery(id+"F0.imprint","IMPRINT",FACE,{"disambiguationData":[TD([[makeQuery(id+"F0.imprint","IMPRINT",EDGE,{"derivedFrom":sQuery(id+"F0.wireOp",EDGE,"E16.3.0")}),1.0]])]});
            var Q12;
            {var subQ0=sQuery(id+"F0.wireOp",EDGE,"E16.4.0");var subQ1=sQuery(id+"F0.wireOp",EDGE,"E1.top");var subQ2=makeQuery(id+"F0.imprint","INTERSECT",VERTEX,{"disambiguationData":[OD(0.0)],"derivedFrom":[subQ1,subQ0]});Q12=makeQuery(id+"F0.imprint","IMPRINT",FACE,{"disambiguationData":[TD([[makeQuery(id+"F0.imprint","IMPRINT",EDGE,{"disambiguationData":[TD([[subQ2,-1.0]])],"derivedFrom":subQ1}),1.0]])]});}
            var Q13;
            {var subQ0=sQuery(id+"F0.wireOp",EDGE,"E16.4.0");var subQ1=sQuery(id+"F0.wireOp",EDGE,"E10.7");var subQ2=makeQuery(id+"F0.imprint","INTERSECT",VERTEX,{"disambiguationData":[OD(0.0)],"derivedFrom":[subQ1,subQ0]});Q13=makeQuery(id+"F0.imprint","IMPRINT",FACE,{"disambiguationData":[TD([[makeQuery(id+"F0.imprint","IMPRINT",EDGE,{"disambiguationData":[TD([[subQ2,-1.0]])],"derivedFrom":subQ1}),-1.0]])]});}
            var Q14;
            {var subQ0=sQuery(id+"F0.wireOp",EDGE,"E16.4.0");var subQ1=sQuery(id+"F0.wireOp",EDGE,"E1.top");var subQ2=makeQuery(id+"F0.imprint","INTERSECT",VERTEX,{"disambiguationData":[OD(0.0)],"derivedFrom":[subQ1,subQ0]});Q14=makeQuery(id+"F0.imprint","IMPRINT",FACE,{"disambiguationData":[TD([[makeQuery(id+"F0.imprint","IMPRINT",EDGE,{"disambiguationData":[TD([[subQ2,-1.0]])],"derivedFrom":subQ1}),-1.0]])]});}
            extrude(context, id + "F2", {"entities" : qUnion([Q0, Q1, Q2, Q3, Q4, Q5, Q6, Q7, Q8, Q9, Q10, Q11, Q12, Q13, Q14]), "depth" : 10 * mm});
        }
        {
            var Q0;
            Q0=makeQuery(id+"F2.opExtrude","SWEPT_BODY",BODY,{"disambiguationData":[OSD([sQuery(id+"F0.wireOp",EDGE,"E15")])]});
            var Q1;
            Q1=makeQuery(id+"F2.opExtrude","SWEPT_BODY",BODY,{"disambiguationData":[OSD([sQuery(id+"F0.wireOp",EDGE,"E16.1.0")])]});
            var Q2;
            Q2=makeQuery(id+"F2.opExtrude","SWEPT_BODY",BODY,{"disambiguationData":[OSD([sQuery(id+"F0.wireOp",EDGE,"E16.2.0")])]});
            var Q3;
            Q3=makeQuery(id+"F2.opExtrude","SWEPT_BODY",BODY,{"disambiguationData":[OSD([sQuery(id+"F0.wireOp",EDGE,"E16.3.0")])]});
            var Q4;
            Q4=makeQuery(id+"F2.opExtrude","SWEPT_BODY",BODY,{"disambiguationData":[OSD([sQuery(id+"F0.wireOp",EDGE,"E16.4.0")])]});
            var Q5;
            Q5=makeQuery(id+"F2.opExtrude","SWEPT_BODY",BODY,{"disambiguationData":[OSD([sQuery(id+"F0.wireOp",EDGE,"E16.5.0")])]});
            var Q6;
            Q6=makeQuery(id+"F2.opExtrude","SWEPT_BODY",BODY,{"disambiguationData":[OSD([sQuery(id+"F0.wireOp",EDGE,"E16.7.0")])]});
            var Q7;
            Q7=makeQuery(id+"F2.opExtrude","SWEPT_BODY",BODY,{"disambiguationData":[OSD([sQuery(id+"F0.wireOp",EDGE,"E16.6.0")])]});
            var Q8;
            Q8=makeQuery(id+"F1.opExtrude","SWEPT_BODY",BODY,{"disambiguationData":[OSD([sQuery(id+"F0.wireOp",EDGE,"E0.bottom"),sQuery(id+"F0.wireOp",EDGE,"E0.top"),sQuery(id+"F0.wireOp",EDGE,"E0.left"),sQuery(id+"F0.wireOp",EDGE,"E0.right"),sQuery(id+"F0.wireOp",EDGE,"E2.filletArc"),sQuery(id+"F0.wireOp",EDGE,"E3.filletArc"),sQuery(id+"F0.wireOp",EDGE,"E4.filletArc"),sQuery(id+"F0.wireOp",EDGE,"E5.filletArc"),sQuery(id+"F0.wireOp",EDGE,"E12.sketch_text.stroke-0"),sQuery(id+"F0.wireOp",EDGE,"E12.sketch_text.stroke-1"),sQuery(id+"F0.wireOp",EDGE,"E12.sketch_text.stroke-2"),sQuery(id+"F0.wireOp",EDGE,"E12.sketch_text.stroke-3"),sQuery(id+"F0.wireOp",EDGE,"E12.sketch_text.stroke-4"),sQuery(id+"F0.wireOp",EDGE,"E12.sketch_text.stroke-5"),sQuery(id+"F0.wireOp",EDGE,"E12.sketch_text.stroke-6"),sQuery(id+"F0.wireOp",EDGE,"E12.sketch_text.stroke-7"),sQuery(id+"F0.wireOp",EDGE,"E12.sketch_text.stroke-8"),sQuery(id+"F0.wireOp",EDGE,"E12.sketch_text.stroke-9"),sQuery(id+"F0.wireOp",EDGE,"E12.sketch_text.stroke-10"),sQuery(id+"F0.wireOp",EDGE,"E12.sketch_text.stroke-11"),sQuery(id+"F0.wireOp",EDGE,"E12.sketch_text.stroke-12"),sQuery(id+"F0.wireOp",EDGE,"E12.sketch_text.stroke-13"),sQuery(id+"F0.wireOp",EDGE,"E12.sketch_text.stroke-14"),sQuery(id+"F0.wireOp",EDGE,"E12.sketch_text.stroke-15"),sQuery(id+"F0.wireOp",EDGE,"E12.sketch_text.stroke-16"),sQuery(id+"F0.wireOp",EDGE,"E12.sketch_text.stroke-17"),sQuery(id+"F0.wireOp",EDGE,"E12.sketch_text.stroke-18"),sQuery(id+"F0.wireOp",EDGE,"E12.sketch_text.stroke-19"),sQuery(id+"F0.wireOp",EDGE,"E12.sketch_text.stroke-20"),sQuery(id+"F0.wireOp",EDGE,"E12.sketch_text.stroke-21"),sQuery(id+"F0.wireOp",EDGE,"E12.sketch_text.stroke-22"),sQuery(id+"F0.wireOp",EDGE,"E12.sketch_text.stroke-23"),sQuery(id+"F0.wireOp",EDGE,"E13.sketch_text.stroke-0"),sQuery(id+"F0.wireOp",EDGE,"E13.sketch_text.stroke-1"),sQuery(id+"F0.wireOp",EDGE,"E13.sketch_text.stroke-2"),sQuery(id+"F0.wireOp",EDGE,"E13.sketch_text.stroke-3"),sQuery(id+"F0.wireOp",EDGE,"E13.sketch_text.stroke-4"),sQuery(id+"F0.wireOp",EDGE,"E13.sketch_text.stroke-5"),sQuery(id+"F0.wireOp",EDGE,"E13.sketch_text.stroke-6"),sQuery(id+"F0.wireOp",EDGE,"E13.sketch_text.stroke-7"),sQuery(id+"F0.wireOp",EDGE,"E13.sketch_text.stroke-8"),sQuery(id+"F0.wireOp",EDGE,"E13.sketch_text.stroke-9"),sQuery(id+"F0.wireOp",EDGE,"E13.sketch_text.stroke-10"),sQuery(id+"F0.wireOp",EDGE,"E13.sketch_text.stroke-11"),sQuery(id+"F0.wireOp",EDGE,"E13.sketch_text.stroke-12"),sQuery(id+"F0.wireOp",EDGE,"E13.sketch_text.stroke-13"),sQuery(id+"F0.wireOp",EDGE,"E13.sketch_text.stroke-14"),sQuery(id+"F0.wireOp",EDGE,"E13.sketch_text.stroke-15"),sQuery(id+"F0.wireOp",EDGE,"E13.sketch_text.stroke-16"),sQuery(id+"F0.wireOp",EDGE,"E13.sketch_text.stroke-17"),sQuery(id+"F0.wireOp",EDGE,"E13.sketch_text.stroke-18"),sQuery(id+"F0.wireOp",EDGE,"E13.sketch_text.stroke-19"),sQuery(id+"F0.wireOp",EDGE,"E13.sketch_text.stroke-20")])]});
            booleanBodies(context, id + "F3", {"operationType" : BooleanOperationType.SUBTRACTION, "tools" : qUnion([Q0, Q1, Q2, Q3, Q4, Q5, Q6, Q7]), "targets" : qUnion([Q8])});
        }
        {
            var Q0;
            {var subQ0=sQuery(id+"F0.wireOp",EDGE,"E18.6.0");var subQ1=sQuery(id+"F0.wireOp",EDGE,"E13.sketch_text.stroke-6");var subQ2=makeQuery(id+"F0.imprint","INTERSECT",VERTEX,{"derivedFrom":[subQ1,subQ0]});Q0=makeQuery(id+"F0.imprint","IMPRINT",FACE,{"disambiguationData":[TD([[makeQuery(id+"F0.imprint","IMPRINT",EDGE,{"disambiguationData":[TD([[subQ2,-1.0]])],"derivedFrom":subQ1}),-1.0]])]});}
            var Q1;
            {var subQ0=sQuery(id+"F0.wireOp",EDGE,"E18.6.0");var subQ1=sQuery(id+"F0.wireOp",EDGE,"E11.5");var subQ2=makeQuery(id+"F0.imprint","INTERSECT",VERTEX,{"disambiguationData":[OD(0.0)],"derivedFrom":[subQ1,subQ0]});Q1=makeQuery(id+"F0.imprint","IMPRINT",FACE,{"disambiguationData":[TD([[makeQuery(id+"F0.imprint","IMPRINT",EDGE,{"disambiguationData":[TD([[subQ2,-1.0]])],"derivedFrom":subQ1}),1.0]])]});}
            var Q2;
            {var subQ1=sQuery(id+"F0.wireOp",EDGE,"E13.sketch_text.stroke-7");Q2=makeQuery(id+"F0.imprint","IMPRINT",FACE,{"disambiguationData":[TD([[makeQuery(id+"F0.imprint","IMPRINT",EDGE,{"derivedFrom":subQ1}),1.0]])]});}
            var Q3;
            {var subQ0=sQuery(id+"F0.wireOp",EDGE,"E13.sketch_text.stroke-7");Q3=makeQuery(id+"F0.imprint","IMPRINT",FACE,{"disambiguationData":[TD([[makeQuery(id+"F0.imprint","IMPRINT",EDGE,{"derivedFrom":subQ0}),-1.0]])]});}
            var Q4;
            {var subQ0=sQuery(id+"F0.wireOp",EDGE,"E16.6.0");var subQ1=sQuery(id+"F0.wireOp",EDGE,"E11.5");var subQ2=makeQuery(id+"F0.imprint","INTERSECT",VERTEX,{"disambiguationData":[OD(1.0)],"derivedFrom":[subQ1,subQ0]});Q4=makeQuery(id+"F0.imprint","IMPRINT",FACE,{"disambiguationData":[TD([[makeQuery(id+"F0.imprint","IMPRINT",EDGE,{"disambiguationData":[TD([[subQ2,-1.0]])],"derivedFrom":subQ1}),1.0]])]});}
            var Q5;
            {var subQ0=sQuery(id+"F0.wireOp",EDGE,"E18.6.0");var subQ1=sQuery(id+"F0.wireOp",EDGE,"E11.5");var subQ2=makeQuery(id+"F0.imprint","INTERSECT",VERTEX,{"disambiguationData":[OD(0.0)],"derivedFrom":[subQ1,subQ0]});Q5=makeQuery(id+"F0.imprint","IMPRINT",FACE,{"disambiguationData":[TD([[makeQuery(id+"F0.imprint","IMPRINT",EDGE,{"disambiguationData":[TD([[subQ2,-1.0]])],"derivedFrom":subQ1}),-1.0]])]});}
            var Q6;
            {var subQ0=sQuery(id+"F0.wireOp",EDGE,"E16.6.0");var subQ1=sQuery(id+"F0.wireOp",EDGE,"E11.5");var subQ2=makeQuery(id+"F0.imprint","INTERSECT",VERTEX,{"disambiguationData":[OD(0.0)],"derivedFrom":[subQ1,subQ0]});Q6=makeQuery(id+"F0.imprint","IMPRINT",FACE,{"disambiguationData":[TD([[makeQuery(id+"F0.imprint","IMPRINT",EDGE,{"disambiguationData":[TD([[subQ2,-1.0]])],"derivedFrom":subQ1}),-1.0]])]});}
            var Q7;
            Q7=makeQuery(id+"F0.imprint","IMPRINT",FACE,{"disambiguationData":[TD([[makeQuery(id+"F0.imprint","IMPRINT",EDGE,{"derivedFrom":sQuery(id+"F0.wireOp",EDGE,"E16.7.0")}),-1.0]])]});
            var Q8;
            {var subQ0=sQuery(id+"F0.wireOp",EDGE,"E18.7.0");var subQ1=sQuery(id+"F0.wireOp",EDGE,"E11.5");var subQ2=makeQuery(id+"F0.imprint","INTERSECT",VERTEX,{"disambiguationData":[OD(0.0)],"derivedFrom":[subQ1,subQ0]});Q8=makeQuery(id+"F0.imprint","IMPRINT",FACE,{"disambiguationData":[TD([[makeQuery(id+"F0.imprint","IMPRINT",EDGE,{"disambiguationData":[TD([[subQ2,-1.0]])],"derivedFrom":subQ1}),1.0]])]});}
            var Q9;
            {var subQ0=sQuery(id+"F0.wireOp",EDGE,"E18.7.0");var subQ1=sQuery(id+"F0.wireOp",EDGE,"E1.right");var subQ2=makeQuery(id+"F0.imprint","INTERSECT",VERTEX,{"disambiguationData":[OD(0.0)],"derivedFrom":[subQ1,subQ0]});Q9=makeQuery(id+"F0.imprint","IMPRINT",FACE,{"disambiguationData":[TD([[makeQuery(id+"F0.imprint","IMPRINT",EDGE,{"disambiguationData":[TD([[subQ2,-1.0]])],"derivedFrom":subQ1}),-1.0]])]});}
            var Q10;
            {var subQ0=sQuery(id+"F0.wireOp",EDGE,"E18.7.0");var subQ1=sQuery(id+"F0.wireOp",EDGE,"E1.right");var subQ2=makeQuery(id+"F0.imprint","INTERSECT",VERTEX,{"disambiguationData":[OD(0.0)],"derivedFrom":[subQ1,subQ0]});Q10=makeQuery(id+"F0.imprint","IMPRINT",FACE,{"disambiguationData":[TD([[makeQuery(id+"F0.imprint","IMPRINT",EDGE,{"disambiguationData":[TD([[subQ2,-1.0]])],"derivedFrom":subQ1}),1.0]])]});}
            var Q11;
            Q11=makeQuery(id+"F0.imprint","IMPRINT",FACE,{"disambiguationData":[TD([[makeQuery(id+"F0.imprint","IMPRINT",EDGE,{"derivedFrom":sQuery(id+"F0.wireOp",EDGE,"E16.7.0")}),1.0]])]});
            var Q12;
            {var subQ0=sQuery(id+"F0.wireOp",EDGE,"E17");var subQ1=sQuery(id+"F0.wireOp",EDGE,"E1.bottom");var subQ2=makeQuery(id+"F0.imprint","INTERSECT",VERTEX,{"disambiguationData":[OD(0.0)],"derivedFrom":[subQ1,subQ0]});Q12=makeQuery(id+"F0.imprint","IMPRINT",FACE,{"disambiguationData":[TD([[makeQuery(id+"F0.imprint","IMPRINT",EDGE,{"disambiguationData":[TD([[subQ2,-1.0]])],"derivedFrom":subQ1}),-1.0]])]});}
            var Q13;
            {var subQ0=sQuery(id+"F0.wireOp",EDGE,"E15");var subQ1=sQuery(id+"F0.wireOp",EDGE,"E1.bottom");var subQ2=makeQuery(id+"F0.imprint","INTERSECT",VERTEX,{"disambiguationData":[OD(0.0)],"derivedFrom":[subQ1,subQ0]});Q13=makeQuery(id+"F0.imprint","IMPRINT",FACE,{"disambiguationData":[TD([[makeQuery(id+"F0.imprint","IMPRINT",EDGE,{"disambiguationData":[TD([[subQ2,-1.0]])],"derivedFrom":subQ1}),-1.0]])]});}
            var Q14;
            {var subQ0=sQuery(id+"F0.wireOp",EDGE,"E15");var subQ1=sQuery(id+"F0.wireOp",EDGE,"E10.2");var subQ2=makeQuery(id+"F0.imprint","INTERSECT",VERTEX,{"disambiguationData":[OD(0.0)],"derivedFrom":[subQ1,subQ0]});Q14=makeQuery(id+"F0.imprint","IMPRINT",FACE,{"disambiguationData":[TD([[makeQuery(id+"F0.imprint","IMPRINT",EDGE,{"disambiguationData":[TD([[subQ2,-1.0]])],"derivedFrom":subQ1}),1.0]])]});}
            var Q15;
            {var subQ0=sQuery(id+"F0.wireOp",EDGE,"E17");var subQ1=sQuery(id+"F0.wireOp",EDGE,"E10.2");var subQ2=makeQuery(id+"F0.imprint","INTERSECT",VERTEX,{"disambiguationData":[OD(0.0)],"derivedFrom":[subQ1,subQ0]});Q15=makeQuery(id+"F0.imprint","IMPRINT",FACE,{"disambiguationData":[TD([[makeQuery(id+"F0.imprint","IMPRINT",EDGE,{"disambiguationData":[TD([[subQ2,-1.0]])],"derivedFrom":subQ1}),1.0]])]});}
            var Q16;
            {var subQ0=sQuery(id+"F0.wireOp",EDGE,"E15");var subQ1=sQuery(id+"F0.wireOp",EDGE,"E1.bottom");var subQ2=makeQuery(id+"F0.imprint","INTERSECT",VERTEX,{"disambiguationData":[OD(1.0)],"derivedFrom":[subQ1,subQ0]});Q16=makeQuery(id+"F0.imprint","IMPRINT",FACE,{"disambiguationData":[TD([[makeQuery(id+"F0.imprint","IMPRINT",EDGE,{"disambiguationData":[TD([[subQ2,-1.0]])],"derivedFrom":subQ1}),1.0]])]});}
            var Q17;
            {var subQ0=sQuery(id+"F0.wireOp",EDGE,"E15");var subQ1=sQuery(id+"F0.wireOp",EDGE,"E1.bottom");var subQ2=makeQuery(id+"F0.imprint","INTERSECT",VERTEX,{"disambiguationData":[OD(0.0)],"derivedFrom":[subQ1,subQ0]});Q17=makeQuery(id+"F0.imprint","IMPRINT",FACE,{"disambiguationData":[TD([[makeQuery(id+"F0.imprint","IMPRINT",EDGE,{"disambiguationData":[TD([[subQ2,-1.0]])],"derivedFrom":subQ1}),1.0]])]});}
            var Q18;
            {var subQ0=sQuery(id+"F0.wireOp",EDGE,"E17");var subQ1=sQuery(id+"F0.wireOp",EDGE,"E1.bottom");var subQ2=makeQuery(id+"F0.imprint","INTERSECT",VERTEX,{"disambiguationData":[OD(0.0)],"derivedFrom":[subQ1,subQ0]});Q18=makeQuery(id+"F0.imprint","IMPRINT",FACE,{"disambiguationData":[TD([[makeQuery(id+"F0.imprint","IMPRINT",EDGE,{"disambiguationData":[TD([[subQ2,-1.0]])],"derivedFrom":subQ1}),1.0]])]});}
            var Q19;
            Q19=makeQuery(id+"F0.imprint","IMPRINT",FACE,{"disambiguationData":[TD([[makeQuery(id+"F0.imprint","IMPRINT",EDGE,{"derivedFrom":sQuery(id+"F0.wireOp",EDGE,"E16.1.0")}),-1.0]])]});
            var Q20;
            Q20=makeQuery(id+"F0.imprint","IMPRINT",FACE,{"disambiguationData":[TD([[makeQuery(id+"F0.imprint","IMPRINT",EDGE,{"derivedFrom":sQuery(id+"F0.wireOp",EDGE,"E16.1.0")}),1.0]])]});
            var Q21;
            {var subQ0=sQuery(id+"F0.wireOp",EDGE,"E18.1.0");var subQ1=sQuery(id+"F0.wireOp",EDGE,"E1.left");var subQ2=makeQuery(id+"F0.imprint","INTERSECT",VERTEX,{"disambiguationData":[OD(0.0)],"derivedFrom":[subQ1,subQ0]});Q21=makeQuery(id+"F0.imprint","IMPRINT",FACE,{"disambiguationData":[TD([[makeQuery(id+"F0.imprint","IMPRINT",EDGE,{"disambiguationData":[TD([[subQ2,-1.0]])],"derivedFrom":subQ1}),-1.0]])]});}
            var Q22;
            {var subQ0=sQuery(id+"F0.wireOp",EDGE,"E18.1.0");var subQ1=sQuery(id+"F0.wireOp",EDGE,"E1.left");var subQ2=makeQuery(id+"F0.imprint","INTERSECT",VERTEX,{"disambiguationData":[OD(0.0)],"derivedFrom":[subQ1,subQ0]});Q22=makeQuery(id+"F0.imprint","IMPRINT",FACE,{"disambiguationData":[TD([[makeQuery(id+"F0.imprint","IMPRINT",EDGE,{"disambiguationData":[TD([[subQ2,-1.0]])],"derivedFrom":subQ1}),1.0]])]});}
            var Q23;
            {var subQ0=sQuery(id+"F0.wireOp",EDGE,"E18.1.0");var subQ1=sQuery(id+"F0.wireOp",EDGE,"E11.1");var subQ2=makeQuery(id+"F0.imprint","INTERSECT",VERTEX,{"disambiguationData":[OD(0.0)],"derivedFrom":[subQ1,subQ0]});Q23=makeQuery(id+"F0.imprint","IMPRINT",FACE,{"disambiguationData":[TD([[makeQuery(id+"F0.imprint","IMPRINT",EDGE,{"disambiguationData":[TD([[subQ2,-1.0]])],"derivedFrom":subQ1}),-1.0]])]});}
            var Q24;
            {var subQ0=sQuery(id+"F0.wireOp",EDGE,"E18.2.0");var subQ1=sQuery(id+"F0.wireOp",EDGE,"E11.1");var subQ2=makeQuery(id+"F0.imprint","INTERSECT",VERTEX,{"disambiguationData":[OD(0.0)],"derivedFrom":[subQ1,subQ0]});Q24=makeQuery(id+"F0.imprint","IMPRINT",FACE,{"disambiguationData":[TD([[makeQuery(id+"F0.imprint","IMPRINT",EDGE,{"disambiguationData":[TD([[subQ2,-1.0]])],"derivedFrom":subQ1}),1.0]])]});}
            var Q25;
            {var subQ0=sQuery(id+"F0.wireOp",EDGE,"E16.2.0");var subQ1=sQuery(id+"F0.wireOp",EDGE,"E11.1");var subQ2=makeQuery(id+"F0.imprint","INTERSECT",VERTEX,{"disambiguationData":[OD(0.0)],"derivedFrom":[subQ1,subQ0]});Q25=makeQuery(id+"F0.imprint","IMPRINT",FACE,{"disambiguationData":[TD([[makeQuery(id+"F0.imprint","IMPRINT",EDGE,{"disambiguationData":[TD([[subQ2,-1.0]])],"derivedFrom":subQ1}),1.0]])]});}
            var Q26;
            {var subQ0=sQuery(id+"F0.wireOp",EDGE,"E16.2.0");var subQ1=sQuery(id+"F0.wireOp",EDGE,"E11.1");var subQ2=makeQuery(id+"F0.imprint","INTERSECT",VERTEX,{"disambiguationData":[OD(0.0)],"derivedFrom":[subQ1,subQ0]});Q26=makeQuery(id+"F0.imprint","IMPRINT",FACE,{"disambiguationData":[TD([[makeQuery(id+"F0.imprint","IMPRINT",EDGE,{"disambiguationData":[TD([[subQ2,-1.0]])],"derivedFrom":subQ1}),-1.0]])]});}
            var Q27;
            {var subQ0=sQuery(id+"F0.wireOp",EDGE,"E18.2.0");var subQ1=sQuery(id+"F0.wireOp",EDGE,"E11.1");var subQ2=makeQuery(id+"F0.imprint","INTERSECT",VERTEX,{"disambiguationData":[OD(0.0)],"derivedFrom":[subQ1,subQ0]});Q27=makeQuery(id+"F0.imprint","IMPRINT",FACE,{"disambiguationData":[TD([[makeQuery(id+"F0.imprint","IMPRINT",EDGE,{"disambiguationData":[TD([[subQ2,-1.0]])],"derivedFrom":subQ1}),-1.0]])]});}
            var Q28;
            Q28=makeQuery(id+"F0.imprint","IMPRINT",FACE,{"disambiguationData":[TD([[makeQuery(id+"F0.imprint","IMPRINT",EDGE,{"derivedFrom":sQuery(id+"F0.wireOp",EDGE,"E16.3.0")}),-1.0]])]});
            var Q29;
            Q29=makeQuery(id+"F0.imprint","IMPRINT",FACE,{"disambiguationData":[TD([[makeQuery(id+"F0.imprint","IMPRINT",EDGE,{"derivedFrom":sQuery(id+"F0.wireOp",EDGE,"E16.3.0")}),1.0]])]});
            var Q30;
            {var subQ0=sQuery(id+"F0.wireOp",EDGE,"E18.3.0");var subQ1=sQuery(id+"F0.wireOp",EDGE,"E11.1");var subQ2=makeQuery(id+"F0.imprint","INTERSECT",VERTEX,{"disambiguationData":[OD(0.0)],"derivedFrom":[subQ1,subQ0]});Q30=makeQuery(id+"F0.imprint","IMPRINT",FACE,{"disambiguationData":[TD([[makeQuery(id+"F0.imprint","IMPRINT",EDGE,{"disambiguationData":[TD([[subQ2,-1.0]])],"derivedFrom":subQ1}),-1.0]])]});}
            var Q31;
            {var subQ0=sQuery(id+"F0.wireOp",EDGE,"E18.3.0");var subQ1=sQuery(id+"F0.wireOp",EDGE,"E1.left");var subQ2=makeQuery(id+"F0.imprint","INTERSECT",VERTEX,{"disambiguationData":[OD(0.0)],"derivedFrom":[subQ1,subQ0]});Q31=makeQuery(id+"F0.imprint","IMPRINT",FACE,{"disambiguationData":[TD([[makeQuery(id+"F0.imprint","IMPRINT",EDGE,{"disambiguationData":[TD([[subQ2,-1.0]])],"derivedFrom":subQ1}),1.0]])]});}
            var Q32;
            {var subQ0=sQuery(id+"F0.wireOp",EDGE,"E18.3.0");var subQ1=sQuery(id+"F0.wireOp",EDGE,"E1.left");var subQ2=makeQuery(id+"F0.imprint","INTERSECT",VERTEX,{"disambiguationData":[OD(0.0)],"derivedFrom":[subQ1,subQ0]});Q32=makeQuery(id+"F0.imprint","IMPRINT",FACE,{"disambiguationData":[TD([[makeQuery(id+"F0.imprint","IMPRINT",EDGE,{"disambiguationData":[TD([[subQ2,-1.0]])],"derivedFrom":subQ1}),-1.0]])]});}
            var Q33;
            {var subQ0=sQuery(id+"F0.wireOp",EDGE,"E18.4.0");var subQ1=sQuery(id+"F0.wireOp",EDGE,"E10.7");var subQ2=makeQuery(id+"F0.imprint","INTERSECT",VERTEX,{"disambiguationData":[OD(0.0)],"derivedFrom":[subQ1,subQ0]});Q33=makeQuery(id+"F0.imprint","IMPRINT",FACE,{"disambiguationData":[TD([[makeQuery(id+"F0.imprint","IMPRINT",EDGE,{"disambiguationData":[TD([[subQ2,-1.0]])],"derivedFrom":subQ1}),-1.0]])]});}
            var Q34;
            {var subQ0=sQuery(id+"F0.wireOp",EDGE,"E16.4.0");var subQ1=sQuery(id+"F0.wireOp",EDGE,"E10.7");var subQ2=makeQuery(id+"F0.imprint","INTERSECT",VERTEX,{"disambiguationData":[OD(0.0)],"derivedFrom":[subQ1,subQ0]});Q34=makeQuery(id+"F0.imprint","IMPRINT",FACE,{"disambiguationData":[TD([[makeQuery(id+"F0.imprint","IMPRINT",EDGE,{"disambiguationData":[TD([[subQ2,-1.0]])],"derivedFrom":subQ1}),-1.0]])]});}
            var Q35;
            {var subQ0=sQuery(id+"F0.wireOp",EDGE,"E18.4.0");var subQ1=sQuery(id+"F0.wireOp",EDGE,"E1.top");var subQ2=makeQuery(id+"F0.imprint","INTERSECT",VERTEX,{"disambiguationData":[OD(0.0)],"derivedFrom":[subQ1,subQ0]});Q35=makeQuery(id+"F0.imprint","IMPRINT",FACE,{"disambiguationData":[TD([[makeQuery(id+"F0.imprint","IMPRINT",EDGE,{"disambiguationData":[TD([[subQ2,-1.0]])],"derivedFrom":subQ1}),1.0]])]});}
            var Q36;
            {var subQ0=sQuery(id+"F0.wireOp",EDGE,"E18.4.0");var subQ1=sQuery(id+"F0.wireOp",EDGE,"E1.top");var subQ2=makeQuery(id+"F0.imprint","INTERSECT",VERTEX,{"disambiguationData":[OD(0.0)],"derivedFrom":[subQ1,subQ0]});Q36=makeQuery(id+"F0.imprint","IMPRINT",FACE,{"disambiguationData":[TD([[makeQuery(id+"F0.imprint","IMPRINT",EDGE,{"disambiguationData":[TD([[subQ2,-1.0]])],"derivedFrom":subQ1}),-1.0]])]});}
            var Q37;
            {var subQ0=sQuery(id+"F0.wireOp",EDGE,"E16.4.0");var subQ1=sQuery(id+"F0.wireOp",EDGE,"E1.top");var subQ2=makeQuery(id+"F0.imprint","INTERSECT",VERTEX,{"disambiguationData":[OD(0.0)],"derivedFrom":[subQ1,subQ0]});Q37=makeQuery(id+"F0.imprint","IMPRINT",FACE,{"disambiguationData":[TD([[makeQuery(id+"F0.imprint","IMPRINT",EDGE,{"disambiguationData":[TD([[subQ2,-1.0]])],"derivedFrom":subQ1}),-1.0]])]});}
            var Q38;
            {var subQ0=sQuery(id+"F0.wireOp",EDGE,"E16.4.0");var subQ1=sQuery(id+"F0.wireOp",EDGE,"E1.top");var subQ2=makeQuery(id+"F0.imprint","INTERSECT",VERTEX,{"disambiguationData":[OD(0.0)],"derivedFrom":[subQ1,subQ0]});Q38=makeQuery(id+"F0.imprint","IMPRINT",FACE,{"disambiguationData":[TD([[makeQuery(id+"F0.imprint","IMPRINT",EDGE,{"disambiguationData":[TD([[subQ2,-1.0]])],"derivedFrom":subQ1}),1.0]])]});}
            var Q39;
            {var subQ0=sQuery(id+"F0.wireOp",EDGE,"E16.4.0");var subQ1=sQuery(id+"F0.wireOp",EDGE,"E1.top");var subQ2=makeQuery(id+"F0.imprint","INTERSECT",VERTEX,{"disambiguationData":[OD(1.0)],"derivedFrom":[subQ1,subQ0]});Q39=makeQuery(id+"F0.imprint","IMPRINT",FACE,{"disambiguationData":[TD([[makeQuery(id+"F0.imprint","IMPRINT",EDGE,{"disambiguationData":[TD([[subQ2,-1.0]])],"derivedFrom":subQ1}),-1.0]])]});}
            var Q40;
            {var subQ0=sQuery(id+"F0.wireOp",EDGE,"E18.5.0");var subQ1=sQuery(id+"F0.wireOp",EDGE,"E1.right");var subQ2=makeQuery(id+"F0.imprint","INTERSECT",VERTEX,{"disambiguationData":[OD(0.0)],"derivedFrom":[subQ1,subQ0]});Q40=makeQuery(id+"F0.imprint","IMPRINT",FACE,{"disambiguationData":[TD([[makeQuery(id+"F0.imprint","IMPRINT",EDGE,{"disambiguationData":[TD([[subQ2,-1.0]])],"derivedFrom":subQ1}),-1.0]])]});}
            var Q41;
            {var subQ0=sQuery(id+"F0.wireOp",EDGE,"E18.5.0");var subQ1=sQuery(id+"F0.wireOp",EDGE,"E1.right");var subQ2=makeQuery(id+"F0.imprint","INTERSECT",VERTEX,{"disambiguationData":[OD(0.0)],"derivedFrom":[subQ1,subQ0]});Q41=makeQuery(id+"F0.imprint","IMPRINT",FACE,{"disambiguationData":[TD([[makeQuery(id+"F0.imprint","IMPRINT",EDGE,{"disambiguationData":[TD([[subQ2,-1.0]])],"derivedFrom":subQ1}),1.0]])]});}
            var Q42;
            Q42=makeQuery(id+"F0.imprint","IMPRINT",FACE,{"disambiguationData":[TD([[makeQuery(id+"F0.imprint","IMPRINT",EDGE,{"derivedFrom":sQuery(id+"F0.wireOp",EDGE,"E16.5.0")}),-1.0]])]});
            var Q43;
            Q43=makeQuery(id+"F0.imprint","IMPRINT",FACE,{"disambiguationData":[TD([[makeQuery(id+"F0.imprint","IMPRINT",EDGE,{"derivedFrom":sQuery(id+"F0.wireOp",EDGE,"E16.5.0")}),1.0]])]});
            var Q44;
            {var subQ0=sQuery(id+"F0.wireOp",EDGE,"E18.5.0");var subQ1=sQuery(id+"F0.wireOp",EDGE,"E11.5");var subQ2=makeQuery(id+"F0.imprint","INTERSECT",VERTEX,{"disambiguationData":[OD(0.0)],"derivedFrom":[subQ1,subQ0]});Q44=makeQuery(id+"F0.imprint","IMPRINT",FACE,{"disambiguationData":[TD([[makeQuery(id+"F0.imprint","IMPRINT",EDGE,{"disambiguationData":[TD([[subQ2,-1.0]])],"derivedFrom":subQ1}),1.0]])]});}
            extrude(context, id + "F4", {"entities" : qUnion([Q0, Q1, Q2, Q3, Q4, Q5, Q6, Q7, Q8, Q9, Q10, Q11, Q12, Q13, Q14, Q15, Q16, Q17, Q18, Q19, Q20, Q21, Q22, Q23, Q24, Q25, Q26, Q27, Q28, Q29, Q30, Q31, Q32, Q33, Q34, Q35, Q36, Q37, Q38, Q39, Q40, Q41, Q42, Q43, Q44]), "depth" : 10 * mm, "hasSecondDirection" : true, "secondDirectionOppositeDirection" : false, "secondDirectionDepth" : 5 * mm});
        }
        {
            var Q0;
            Q0=makeQuery(id+"F4.opExtrude","SWEPT_BODY",BODY,{"disambiguationData":[OSD([sQuery(id+"F0.wireOp",EDGE,"E18.7.0")])]});
            var Q1;
            Q1=makeQuery(id+"F4.opExtrude","SWEPT_BODY",BODY,{"disambiguationData":[OSD([sQuery(id+"F0.wireOp",EDGE,"E18.6.0")])]});
            var Q2;
            Q2=makeQuery(id+"F4.opExtrude","SWEPT_BODY",BODY,{"disambiguationData":[OSD([sQuery(id+"F0.wireOp",EDGE,"E18.5.0")])]});
            var Q3;
            Q3=makeQuery(id+"F4.opExtrude","SWEPT_BODY",BODY,{"disambiguationData":[OSD([sQuery(id+"F0.wireOp",EDGE,"E18.4.0")])]});
            var Q4;
            Q4=makeQuery(id+"F4.opExtrude","SWEPT_BODY",BODY,{"disambiguationData":[OSD([sQuery(id+"F0.wireOp",EDGE,"E18.3.0")])]});
            var Q5;
            Q5=makeQuery(id+"F4.opExtrude","SWEPT_BODY",BODY,{"disambiguationData":[OSD([sQuery(id+"F0.wireOp",EDGE,"E18.2.0")])]});
            var Q6;
            Q6=makeQuery(id+"F4.opExtrude","SWEPT_BODY",BODY,{"disambiguationData":[OSD([sQuery(id+"F0.wireOp",EDGE,"E18.1.0")])]});
            var Q7;
            Q7=makeQuery(id+"F1.opExtrude","SWEPT_BODY",BODY,{"disambiguationData":[OSD([sQuery(id+"F0.wireOp",EDGE,"E0.bottom"),sQuery(id+"F0.wireOp",EDGE,"E0.top"),sQuery(id+"F0.wireOp",EDGE,"E0.left"),sQuery(id+"F0.wireOp",EDGE,"E0.right"),sQuery(id+"F0.wireOp",EDGE,"E2.filletArc"),sQuery(id+"F0.wireOp",EDGE,"E3.filletArc"),sQuery(id+"F0.wireOp",EDGE,"E4.filletArc"),sQuery(id+"F0.wireOp",EDGE,"E5.filletArc"),sQuery(id+"F0.wireOp",EDGE,"E12.sketch_text.stroke-0"),sQuery(id+"F0.wireOp",EDGE,"E12.sketch_text.stroke-1"),sQuery(id+"F0.wireOp",EDGE,"E12.sketch_text.stroke-2"),sQuery(id+"F0.wireOp",EDGE,"E12.sketch_text.stroke-3"),sQuery(id+"F0.wireOp",EDGE,"E12.sketch_text.stroke-4"),sQuery(id+"F0.wireOp",EDGE,"E12.sketch_text.stroke-5"),sQuery(id+"F0.wireOp",EDGE,"E12.sketch_text.stroke-6"),sQuery(id+"F0.wireOp",EDGE,"E12.sketch_text.stroke-7"),sQuery(id+"F0.wireOp",EDGE,"E12.sketch_text.stroke-8"),sQuery(id+"F0.wireOp",EDGE,"E12.sketch_text.stroke-9"),sQuery(id+"F0.wireOp",EDGE,"E12.sketch_text.stroke-10"),sQuery(id+"F0.wireOp",EDGE,"E12.sketch_text.stroke-11"),sQuery(id+"F0.wireOp",EDGE,"E12.sketch_text.stroke-12"),sQuery(id+"F0.wireOp",EDGE,"E12.sketch_text.stroke-13"),sQuery(id+"F0.wireOp",EDGE,"E12.sketch_text.stroke-14"),sQuery(id+"F0.wireOp",EDGE,"E12.sketch_text.stroke-15"),sQuery(id+"F0.wireOp",EDGE,"E12.sketch_text.stroke-16"),sQuery(id+"F0.wireOp",EDGE,"E12.sketch_text.stroke-17"),sQuery(id+"F0.wireOp",EDGE,"E12.sketch_text.stroke-18"),sQuery(id+"F0.wireOp",EDGE,"E12.sketch_text.stroke-19"),sQuery(id+"F0.wireOp",EDGE,"E12.sketch_text.stroke-20"),sQuery(id+"F0.wireOp",EDGE,"E12.sketch_text.stroke-21"),sQuery(id+"F0.wireOp",EDGE,"E12.sketch_text.stroke-22"),sQuery(id+"F0.wireOp",EDGE,"E12.sketch_text.stroke-23"),sQuery(id+"F0.wireOp",EDGE,"E13.sketch_text.stroke-0"),sQuery(id+"F0.wireOp",EDGE,"E13.sketch_text.stroke-1"),sQuery(id+"F0.wireOp",EDGE,"E13.sketch_text.stroke-2"),sQuery(id+"F0.wireOp",EDGE,"E13.sketch_text.stroke-3"),sQuery(id+"F0.wireOp",EDGE,"E13.sketch_text.stroke-4"),sQuery(id+"F0.wireOp",EDGE,"E13.sketch_text.stroke-5"),sQuery(id+"F0.wireOp",EDGE,"E13.sketch_text.stroke-6"),sQuery(id+"F0.wireOp",EDGE,"E13.sketch_text.stroke-7"),sQuery(id+"F0.wireOp",EDGE,"E13.sketch_text.stroke-8"),sQuery(id+"F0.wireOp",EDGE,"E13.sketch_text.stroke-9"),sQuery(id+"F0.wireOp",EDGE,"E13.sketch_text.stroke-10"),sQuery(id+"F0.wireOp",EDGE,"E13.sketch_text.stroke-11"),sQuery(id+"F0.wireOp",EDGE,"E13.sketch_text.stroke-12"),sQuery(id+"F0.wireOp",EDGE,"E13.sketch_text.stroke-13"),sQuery(id+"F0.wireOp",EDGE,"E13.sketch_text.stroke-14"),sQuery(id+"F0.wireOp",EDGE,"E13.sketch_text.stroke-15"),sQuery(id+"F0.wireOp",EDGE,"E13.sketch_text.stroke-16"),sQuery(id+"F0.wireOp",EDGE,"E13.sketch_text.stroke-17"),sQuery(id+"F0.wireOp",EDGE,"E13.sketch_text.stroke-18"),sQuery(id+"F0.wireOp",EDGE,"E13.sketch_text.stroke-19"),sQuery(id+"F0.wireOp",EDGE,"E13.sketch_text.stroke-20")])]});
            booleanBodies(context, id + "F5", {"operationType" : BooleanOperationType.SUBTRACTION, "tools" : qUnion([Q0, Q1, Q2, Q3, Q4, Q5, Q6]), "targets" : qUnion([Q7])});
        }
        {
            var Q0;
            Q0=makeQuery(id+"F4.opExtrude","SWEPT_BODY",BODY,{"disambiguationData":[OSD([sQuery(id+"F0.wireOp",EDGE,"E17")])]});
            deleteBodies(context, id + "F6", {"entities" : qUnion([Q0])});
        }
        {
            var Q0;
            {var subQ15=sQuery(id+"F0.wireOp",EDGE,"E6.filletArc");Q0=makeQuery(id+"F0.imprint","IMPRINT",FACE,{"disambiguationData":[TD([[makeQuery(id+"F0.imprint","IMPRINT",EDGE,{"derivedFrom":subQ15}),1.0]])]});}
            var Q1;
            {var subQ0=sQuery(id+"F0.wireOp",EDGE,"E17");var subQ1=sQuery(id+"F0.wireOp",EDGE,"E1.bottom");var subQ2=makeQuery(id+"F0.imprint","INTERSECT",VERTEX,{"disambiguationData":[OD(0.0)],"derivedFrom":[subQ1,subQ0]});Q1=makeQuery(id+"F0.imprint","IMPRINT",FACE,{"disambiguationData":[TD([[makeQuery(id+"F0.imprint","IMPRINT",EDGE,{"disambiguationData":[TD([[subQ2,-1.0]])],"derivedFrom":subQ1}),-1.0]])]});}
            extrude(context, id + "F7", {"entities" : qUnion([Q0, Q1]), "operationType" : NewBodyOperationType.ADD, "depth" : 30 * mm});
        }
        {
            var Q0;
            Q0=qCreatedBy(makeId("Right.planeOp"),FACE);
            var sketch = newSketch(context, id + "F8", { "sketchPlane" : qUnion([Q0])});
            skCircle(sketch, "E20", {"center": v(5, 23) * mm, "radius": 2.6 * mm});
            skSolve(sketch);
        }
        {
            var Q0;
            Q0=makeQuery(id+"F8.imprint","IMPRINT",FACE,{"disambiguationData":[TD([[makeQuery(id+"F8.imprint","IMPRINT",EDGE,{"derivedFrom":sQuery(id+"F8.wireOp",EDGE,"E20")}),1.0]])]});
            extrude(context, id + "F9", {"entities" : qUnion([Q0]), "depth" : 25 * mm, "symmetric" : true});
        }
        {
            var Q0;
            Q0=makeQuery(id+"F9.opExtrude","SWEPT_BODY",BODY,{"disambiguationData":[OSD([sQuery(id+"F8.wireOp",EDGE,"E20")])]});
            var Q1;
            Q1=makeQuery(id+"F1.opExtrude","SWEPT_BODY",BODY,{"disambiguationData":[OSD([sQuery(id+"F0.wireOp",EDGE,"E0.bottom"),sQuery(id+"F0.wireOp",EDGE,"E0.top"),sQuery(id+"F0.wireOp",EDGE,"E0.left"),sQuery(id+"F0.wireOp",EDGE,"E0.right"),sQuery(id+"F0.wireOp",EDGE,"E2.filletArc"),sQuery(id+"F0.wireOp",EDGE,"E3.filletArc"),sQuery(id+"F0.wireOp",EDGE,"E4.filletArc"),sQuery(id+"F0.wireOp",EDGE,"E5.filletArc"),sQuery(id+"F0.wireOp",EDGE,"E12.sketch_text.stroke-0"),sQuery(id+"F0.wireOp",EDGE,"E12.sketch_text.stroke-1"),sQuery(id+"F0.wireOp",EDGE,"E12.sketch_text.stroke-2"),sQuery(id+"F0.wireOp",EDGE,"E12.sketch_text.stroke-3"),sQuery(id+"F0.wireOp",EDGE,"E12.sketch_text.stroke-4"),sQuery(id+"F0.wireOp",EDGE,"E12.sketch_text.stroke-5"),sQuery(id+"F0.wireOp",EDGE,"E12.sketch_text.stroke-6"),sQuery(id+"F0.wireOp",EDGE,"E12.sketch_text.stroke-7"),sQuery(id+"F0.wireOp",EDGE,"E12.sketch_text.stroke-8"),sQuery(id+"F0.wireOp",EDGE,"E12.sketch_text.stroke-9"),sQuery(id+"F0.wireOp",EDGE,"E12.sketch_text.stroke-10"),sQuery(id+"F0.wireOp",EDGE,"E12.sketch_text.stroke-11"),sQuery(id+"F0.wireOp",EDGE,"E12.sketch_text.stroke-12"),sQuery(id+"F0.wireOp",EDGE,"E12.sketch_text.stroke-13"),sQuery(id+"F0.wireOp",EDGE,"E12.sketch_text.stroke-14"),sQuery(id+"F0.wireOp",EDGE,"E12.sketch_text.stroke-15"),sQuery(id+"F0.wireOp",EDGE,"E12.sketch_text.stroke-16"),sQuery(id+"F0.wireOp",EDGE,"E12.sketch_text.stroke-17"),sQuery(id+"F0.wireOp",EDGE,"E12.sketch_text.stroke-18"),sQuery(id+"F0.wireOp",EDGE,"E12.sketch_text.stroke-19"),sQuery(id+"F0.wireOp",EDGE,"E12.sketch_text.stroke-20"),sQuery(id+"F0.wireOp",EDGE,"E12.sketch_text.stroke-21"),sQuery(id+"F0.wireOp",EDGE,"E12.sketch_text.stroke-22"),sQuery(id+"F0.wireOp",EDGE,"E12.sketch_text.stroke-23"),sQuery(id+"F0.wireOp",EDGE,"E13.sketch_text.stroke-0"),sQuery(id+"F0.wireOp",EDGE,"E13.sketch_text.stroke-1"),sQuery(id+"F0.wireOp",EDGE,"E13.sketch_text.stroke-2"),sQuery(id+"F0.wireOp",EDGE,"E13.sketch_text.stroke-3"),sQuery(id+"F0.wireOp",EDGE,"E13.sketch_text.stroke-4"),sQuery(id+"F0.wireOp",EDGE,"E13.sketch_text.stroke-5"),sQuery(id+"F0.wireOp",EDGE,"E13.sketch_text.stroke-6"),sQuery(id+"F0.wireOp",EDGE,"E13.sketch_text.stroke-7"),sQuery(id+"F0.wireOp",EDGE,"E13.sketch_text.stroke-8"),sQuery(id+"F0.wireOp",EDGE,"E13.sketch_text.stroke-9"),sQuery(id+"F0.wireOp",EDGE,"E13.sketch_text.stroke-10"),sQuery(id+"F0.wireOp",EDGE,"E13.sketch_text.stroke-11"),sQuery(id+"F0.wireOp",EDGE,"E13.sketch_text.stroke-12"),sQuery(id+"F0.wireOp",EDGE,"E13.sketch_text.stroke-13"),sQuery(id+"F0.wireOp",EDGE,"E13.sketch_text.stroke-14"),sQuery(id+"F0.wireOp",EDGE,"E13.sketch_text.stroke-15"),sQuery(id+"F0.wireOp",EDGE,"E13.sketch_text.stroke-16"),sQuery(id+"F0.wireOp",EDGE,"E13.sketch_text.stroke-17"),sQuery(id+"F0.wireOp",EDGE,"E13.sketch_text.stroke-18"),sQuery(id+"F0.wireOp",EDGE,"E13.sketch_text.stroke-19"),sQuery(id+"F0.wireOp",EDGE,"E13.sketch_text.stroke-20")])]});
            booleanBodies(context, id + "F10", {"operationType" : BooleanOperationType.SUBTRACTION, "tools" : qUnion([Q0]), "targets" : qUnion([Q1])});
        }
        {
            var Q0;
            Q0=makeQuery(id+"F0.imprint","IMPRINT",FACE,{"disambiguationData":[TD([[makeQuery(id+"F0.imprint","IMPRINT",EDGE,{"derivedFrom":sQuery(id+"F0.wireOp",EDGE,"E0.bottom")}),-1.0]])]});
            extrude(context, id + "F11", {"entities" : qUnion([Q0]), "operationType" : NewBodyOperationType.REMOVE, "depth" : 10 * mm, "hasSecondDirection" : true, "secondDirectionOppositeDirection" : false, "secondDirectionDepth" : 5 * mm});
        }
    });
